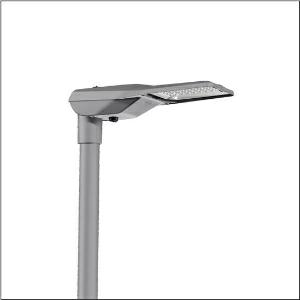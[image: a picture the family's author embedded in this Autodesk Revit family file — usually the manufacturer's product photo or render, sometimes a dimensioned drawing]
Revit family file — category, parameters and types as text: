
# Revit family: streetlight_sl_21_iq_mini___st0_8a_5xe2c31y08hb_5d56
name_source: partatom
category: Lighting Fixtures
units: mm (PartAtom-declared; Revit-internal decimal feet)

## family parameters
Cut with Voids When Loaded = No
Host = Face
Light Source = No
Part Type = Normal
Room Calculation Point = No
Round Connector Dimension = Use Diameter
Shared = No

## types (1)
- --- (1 x LED, 9750 lm, 71 W, 3000K)
    Apparent Load = 71 VA
    CIE Flux Codes = 38 75 97 100 100
    Color Rendering = 70
    Color Temperature = 3000K
    Default Elevation = 1800 mm
    Description = Streetlight SL 21 iQ mini, mast luminaire, primary light control with lens, of PMMA, primary optical cover: cover, of toughened safety glass, transparent, light distribution: ST0.8a, light emission: direct distribution, primary light characteristic: asymmetric, installation type: post-top, side-entry, LED, High Power LED, rated luminous flux: 9.750lm, luminous efficacy: 137lm/W, light colour: 730, colour temperature: 3000K, control: pre-setting: logarithmic dimming characteristic, Street-Remote, Auto-Match, Temp-Guard, Lumen-Switch, Night-Set, Smart-Wire, Light-Fading, Desk-Remote (wireless, voltage-free reading and setting of iQ features in the workshop via application-optimized NFC function/RFID function), optimised constant luminous flux control (CLO 2.0), mains connection: 220..240V, AC, 50/60Hz, start of lifetime: 71W, end of service life: 75W, reduction: 30W, luminaire housing, of diecast aluminium, powder-coated, Siteco® metallic grey (DB 702S), corrosivity category C5 mid according to DIN EN ISO 12944, please order mast flange separately, inclination adjustable: 0°, 5°, 10°, 15°, sealing non-destructively replaceable, multi-level sealing system, length: 628mm, width: 235mm, height: 110mm, mast flange for spigot size: 42mm (side-entry): 5XC10008XM4, 60/48mm (side-entry/post-top): 5XC10108XM2, 76/60mm (side-entry/post-top): 5XC10108XM1, Smart Interface below and above, protection rating (complete): IP66, insulation class (complete): insulation class II (safety insulation), certification: CE, ENEC, ENEC+, VDE, impact resistance: IK09, permissible operating ambient temperature for outdoor applications: -40..+50°C, standard-compliant lighting for roads and squares, packaging unit: 1 piece

Light Distribution: ST0.8a
    Height = 110 mm
    Lamp = 1 x LED
    Lamp Light Flux = 9750 lm
    Lamp Power = 71 W
    Lamp count = 1
    Length = 625 mm
    Luminous efficacy = 137 lm/W
    Manufacturer = Siteco
    ModVariant = No
    Model = 5XE2C31Y08HB
    Number of Poles = 1
    OnlyDefault = Yes
    Power Factor = 1
    Product Name = Streetlight SL 21 iQ mini | ST0.8a
    Product group = mast luminaire | pylon top
    ProductGroupID = 6100
    Protection Class = Protection class II
    Protection Degree = IP 66
    RLX_Detail_Level = 1
    RLX_Emergency_Light_Flux = 0 lm
    RLX_Emergency_Type = 0
    RLX_Emergency_Type_DB = No
    RlxData = <blob elided: 92877 chars, md5=c7bfa9ac>
    Socket = socket
    Standby Power = 0 W
    System Light Flux = 9750 lm
    System Power = 71 W
    Type Comments = factory setting: luminous flux: 100 % | dim-lin: 254 | 716 mA
    Type Image = l_1003514.jpg
    URL = http://relux.com
    VarID = @adj_082155
    Voltage = 0 V
    Weight = 0.00 kg
    Width = 234 mm

## geometry (parser evidence)
native form markers: Blend x4, Sweep x13
no freeform markers — native parametric forms only
